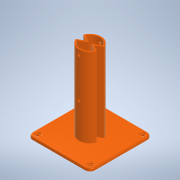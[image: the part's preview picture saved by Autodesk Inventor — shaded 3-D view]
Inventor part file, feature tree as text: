
AUTODESK INVENTOR PART (.ipt)
format: ipt  version: 2020 (Build 240168000, 168)  size: 222,720 bytes
history: native  units: in
note: dims shown in document units (in); Inventor stores cm internally (conversion verified against a paired STEP export)
features: extrude x7, sketch x7, mirror x2, fillet x2, shell x1, projected_geometry x1
ambient origin geometry x8: Origin, YZ Plane, XZ Plane, XY Plane, X Axis, Y Axis, Z Axis, Center Point
bodies: Solid1 (feature_tree)
feature tree (20):
  extrude  "Extrusion1"  Depth=0.2in
  shell  "Shell1"  Thickness=30.0deg
  extrude  "Extrusion2"  Depth=4.0in
  extrude  "Extrusion3"  Depth=3.1496in
  extrude  "Extrusion4"  Depth=0.125in TaperAngle=0.0deg
  extrude  "Extrusion5"  Depth=0.125in
  extrude  "Extrusion6"  Depth=4.0in TaperAngle=0.0deg
  extrude  "Extrusion7"  Depth=0.025in
  mirror  "Mirror1"
  mirror  "Mirror2"
  fillet  "Fillet1"  Radius=4.0in
  fillet  "Fillet2"  Radius=0.1339in
  sketch  "Sketch1"  dims[d0=1.125in d1=0.2in d2=30.0deg]
  sketch  "Sketch2"  dims[d3=4.0in d4=0.0in d5=0.0669in]
  sketch  "Sketch3"  dims[d6=3.1496in d7=3.1496in]
  projected_geometry  "Projected Loop1"
  sketch  "Sketch4"  dims[d9=0.25in d10=0.125in d11=0.0in]
  sketch  "Sketch5"  dims[d12=0.0669in d13=0.0in d14=0.125in]
  sketch  "Sketch6"  dims[d15=1.75in d16=4.0in d17=0.0in]
  sketch  "Sketch7"  dims[d18=0.125in d19=3.75in d20=4.0in d21=2.0in d22=0.0in d23=0.0in d24=0.1339in d25=1.0in d26=0.0in d27=0.25in d28=0.05in d29=0.0in d30=0.0625in d31=0.025in]
